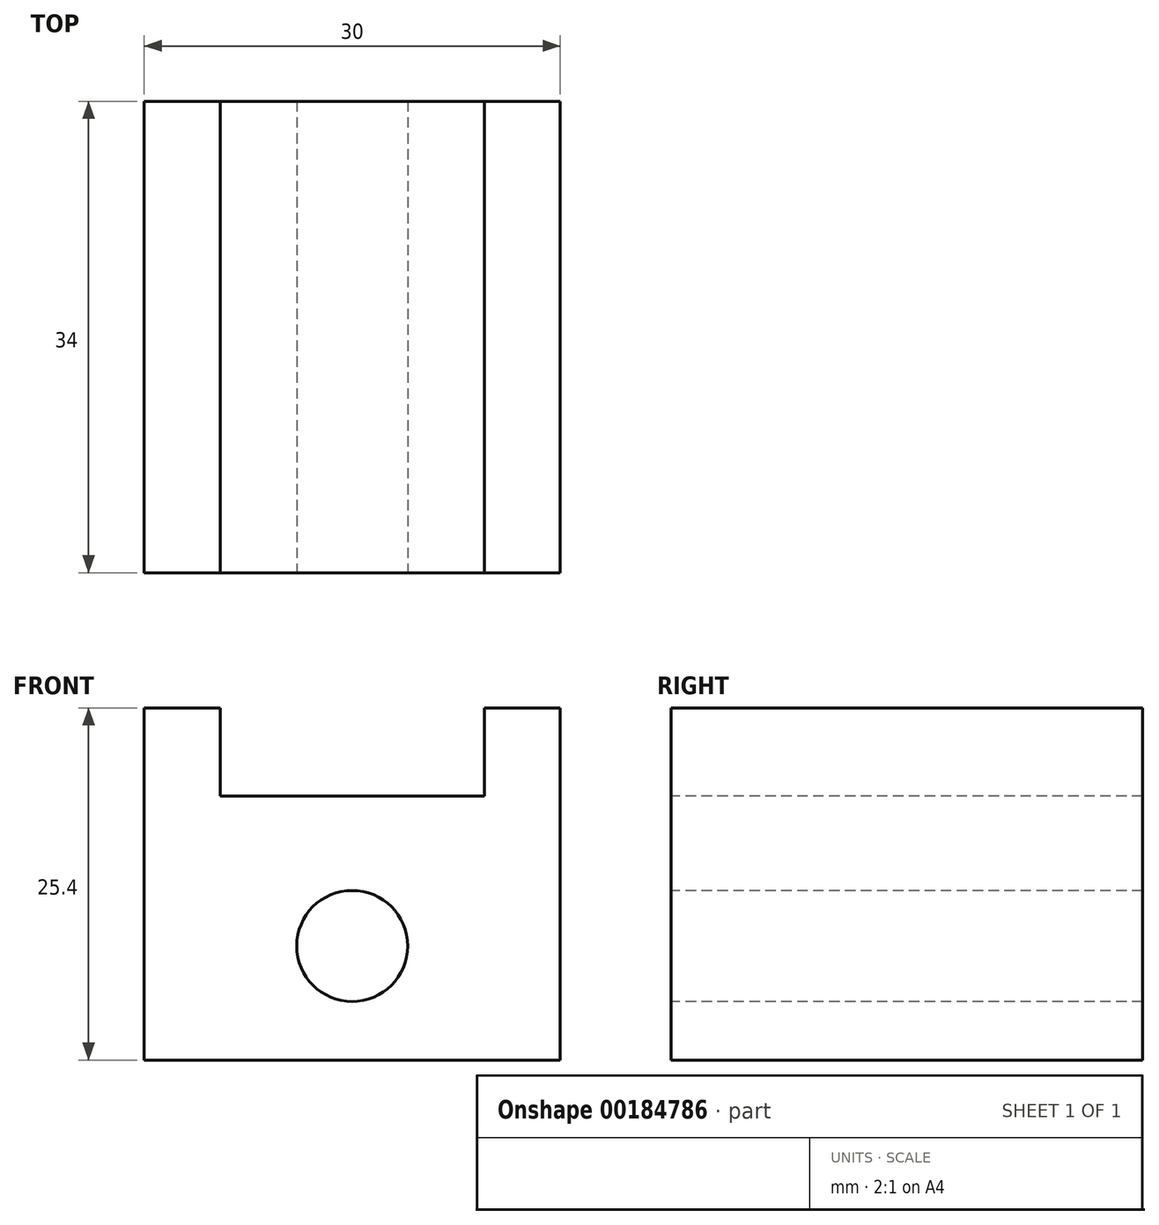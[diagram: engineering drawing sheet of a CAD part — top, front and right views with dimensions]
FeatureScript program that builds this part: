
annotation { "Feature Type Name" : "Feature", "Feature Type Description" : "" }
export const myFeature = defineFeature(function(context is Context, id is Id, definition is map)
    precondition{}
    {
        {
            var Q0;
            Q0=qCreatedBy(makeId("Top.planeOp"),FACE);
            var sketch = newSketch(context, id + "F0", { "sketchPlane" : qUnion([Q0])});
            skLineSegment(sketch, "E0.bottom", {"start": v(15, 17) * mm, "end": v(-15, 17) * mm});
            skLineSegment(sketch, "E0.top", {"start": v(15, -17) * mm, "end": v(-15, -17) * mm});
            skLineSegment(sketch, "E0.left", {"start": v(15, 17) * mm, "end": v(15, -17) * mm});
            skLineSegment(sketch, "E0.right", {"start": v(-15, 17) * mm, "end": v(-15, -17) * mm});
            skPoint(sketch, "E0.middle", {"position": v(0, 0) * mm});
            skSolve(sketch);
        }
        {
            var Q0;
            Q0=makeQuery(id+"F0.imprint","IMPRINT",FACE,{"disambiguationData":[TD([[makeQuery(id+"F0.imprint","IMPRINT",EDGE,{"derivedFrom":sQuery(id+"F0.wireOp",EDGE,"E0.bottom")}),1.0]])]});
            extrude(context, id + "F1", {"entities" : qUnion([Q0]), "depth" : 25.4 * mm});
        }
        {
            var Q0;
            Q0=makeQuery(id+"F1.opExtrude","SWEPT_FACE",FACE,{"disambiguationData":[OSD([sQuery(id+"F0.wireOp",EDGE,"E0.top")])]});
            var sketch = newSketch(context, id + "F2", { "sketchPlane" : qUnion([Q0])});
            skCircle(sketch, "E1", {"center": v(0, 8.22) * mm, "radius": 4 * mm});
            skSolve(sketch);
        }
        {
            var Q0;
            Q0=makeQuery(id+"F2.imprint","IMPRINT",FACE,{"disambiguationData":[TD([[makeQuery(id+"F2.imprint","IMPRINT",EDGE,{"derivedFrom":sQuery(id+"F2.wireOp",EDGE,"E1")}),1.0]])]});
            extrude(context, id + "F3", {"entities" : qUnion([Q0]), "operationType" : NewBodyOperationType.REMOVE, "endBound" : BoundingType.THROUGH_ALL, "oppositeDirection" : true, "depth" : 25.4 * mm});
        }
        {
            var Q0;
            Q0=makeQuery(id+"F1.opExtrude","CAP_FACE",FACE,{"disambiguationData":[OSD([sQuery(id+"F0.wireOp",EDGE,"E0.bottom"),sQuery(id+"F0.wireOp",EDGE,"E0.top"),sQuery(id+"F0.wireOp",EDGE,"E0.left"),sQuery(id+"F0.wireOp",EDGE,"E0.right")])],"isStart":false});
            var sketch = newSketch(context, id + "F4", { "sketchPlane" : qUnion([Q0])});
            skLineSegment(sketch, "E2.bottom", {"start": v(9.53, 17) * mm, "end": v(-9.53, 17) * mm});
            skLineSegment(sketch, "E2.top", {"start": v(9.53, -17) * mm, "end": v(-9.53, -17) * mm});
            skLineSegment(sketch, "E2.left", {"start": v(9.53, 17) * mm, "end": v(9.53, -17) * mm});
            skLineSegment(sketch, "E2.right", {"start": v(-9.53, 17) * mm, "end": v(-9.53, -17) * mm});
            skPoint(sketch, "E2.middle", {"position": v(0, 0) * mm});
            skSolve(sketch);
        }
        {
            var Q0;
            Q0=qSketchRegion(id+"F4",true);
            extrude(context, id + "F5", {"entities" : qUnion([Q0]), "operationType" : NewBodyOperationType.REMOVE, "oppositeDirection" : true, "depth" : 6.35 * mm});
        }
    });
